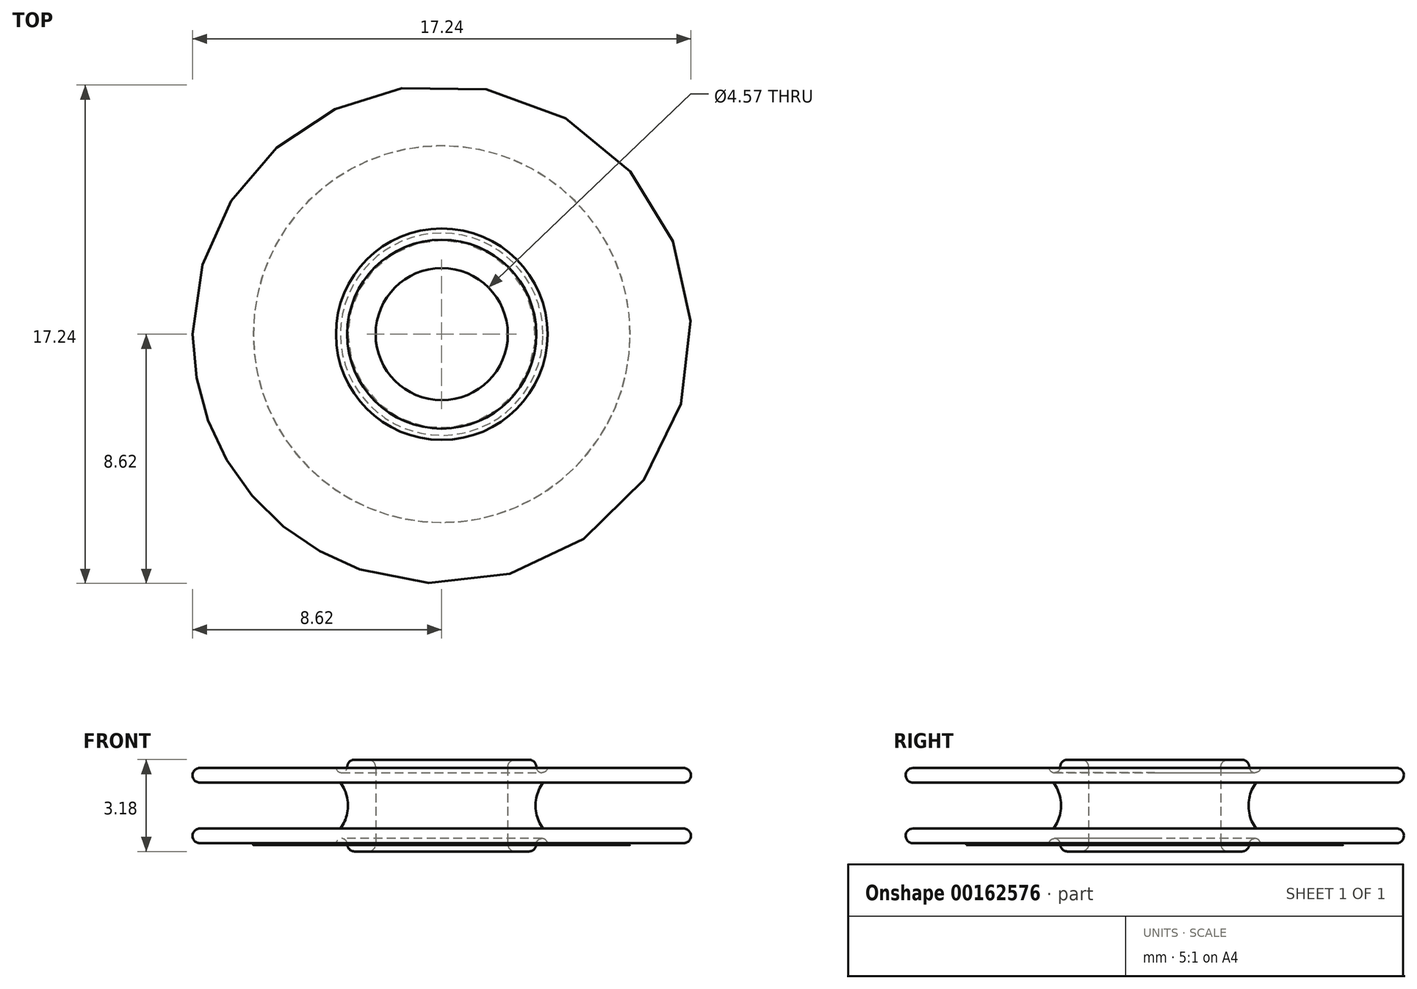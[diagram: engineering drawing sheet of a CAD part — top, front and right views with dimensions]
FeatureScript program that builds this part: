
annotation { "Feature Type Name" : "Feature", "Feature Type Description" : "" }
export const myFeature = defineFeature(function(context is Context, id is Id, definition is map)
    precondition{}
    {
        {
            var Q0;
            Q0=qCreatedBy(makeId("Front.planeOp"),FACE);
            var sketch = newSketch(context, id + "F0", { "sketchPlane" : qUnion([Q0])});
            skPoint(sketch, "E0.end.orphan", {"position": v(8.13, 3.13) * mm});
            skPoint(sketch, "E1.start.orphan", {"position": v(1.92, 6.45) * mm});
            skPoint(sketch, "E2.orphan", {"position": v(1.92, 3.4) * mm});
            skLineSegment(sketch, "E3", {"start": v(10.16, 2.03) * mm, "end": v(10.16, 2.03) * mm});
            skPoint(sketch, "E4.orphan", {"position": v(8.13, 0) * mm});
            skPoint(sketch, "E5.end.orphan", {"position": v(-8.13, 0) * mm});
            skPoint(sketch, "E6.visualSharp", {"position": v(2.67, 2.67) * mm});
            skPoint(sketch, "E7.visualSharp", {"position": v(1.3, 4.1) * mm});
            skPoint(sketch, "E8.visualSharp", {"position": v(10.16, 2.03) * mm});
            skPoint(sketch, "E9.visualSharp", {"position": v(1.3, 0.1) * mm});
            skLineSegment(sketch, "E10", {"start": v(1.56, 4.1) * mm, "end": v(1.56, 4.1) * mm});
            skLineSegment(sketch, "E11", {"start": v(2.92, 1.7) * mm, "end": v(2.92, 1.7) * mm});
            skPoint(sketch, "E12.visualSharp", {"position": v(2.43, 4.1) * mm});
            skPoint(sketch, "E13.end.orphan", {"position": v(5.24, 0.6) * mm});
            skPoint(sketch, "E13.start.orphan", {"position": v(5.24, -0.32) * mm});
            skLineSegment(sketch, "E14", {"start": v(2.29, 2.92) * mm, "end": v(2.29, 0.25) * mm});
            skLineSegment(sketch, "E15", {"start": v(3.02, 3.18) * mm, "end": v(2.54, 3.18) * mm});
            skArc(sketch, "E16.filletArc", {"start": v(3.27, 2.92) * mm, "mid": v(3.2, 3.1) * mm, "end": v(3.02, 3.18) * mm});
            skPoint(sketch, "E17.visualSharp", {"position": v(2.29, 3.18) * mm});
            skArc(sketch, "E17.filletArc", {"start": v(2.54, 3.18) * mm, "mid": v(2.36, 3.1) * mm, "end": v(2.29, 2.92) * mm});
            skPoint(sketch, "E18.orphan", {"position": v(5.7, 4.63) * mm});
            skPoint(sketch, "E19.orphan", {"position": v(5.7, 4.44) * mm});
            skLineSegment(sketch, "E20", {"start": v(6.52, 0.24) * mm, "end": v(6.51, 0.22) * mm});
            skPoint(sketch, "E21.visualSharp", {"position": v(2.29, 0) * mm});
            skPoint(sketch, "E22.visualSharp", {"position": v(3.24, 0) * mm});
            skPoint(sketch, "E23.visualSharp", {"position": v(3.27, 2.68) * mm});
            skPoint(sketch, "E24.visualSharp", {"position": v(3.38, 1.58) * mm});
            skPoint(sketch, "E25.visualSharp", {"position": v(3.24, 1.24) * mm});
            skPoint(sketch, "E26.visualSharp", {"position": v(9.55, 4.38) * mm});
            skPoint(sketch, "E27.visualSharp", {"position": v(9.7, 4.34) * mm});
            skPoint(sketch, "E28.visualSharp", {"position": v(6.6, 0.46) * mm});
            skArc(sketch, "E28.filletArc", {"start": v(6.51, 0.22) * mm, "mid": v(6.51, 0.22) * mm, "end": v(6.52, 0.23) * mm});
            skPoint(sketch, "E29.visualSharp", {"position": v(6.44, 0) * mm});
            skArc(sketch, "E29.filletArc", {"start": v(6.52, 0.23) * mm, "mid": v(6.52, 0.23) * mm, "end": v(6.52, 0.24) * mm});
            skLineSegment(sketch, "E30", {"start": v(8.36, 2.9) * mm, "end": v(3.66, 2.9) * mm});
            skArc(sketch, "E31", {"start": v(8.36, 2.38) * mm, "mid": v(8.62, 2.64) * mm, "end": v(8.36, 2.9) * mm});
            skLineSegment(sketch, "E32", {"start": v(8.36, 2.38) * mm, "end": v(3.5, 2.38) * mm});
            skPoint(sketch, "E33.orphan", {"position": v(8.64, 2.9) * mm});
            skArc(sketch, "E34", {"start": v(3.22, 1.26) * mm, "mid": v(3.23, 1.25) * mm, "end": v(3.24, 1.24) * mm});
            skArc(sketch, "E35", {"start": v(3.27, 2.92) * mm, "mid": v(3.45, 2.73) * mm, "end": v(3.66, 2.9) * mm});
            skLineSegment(sketch, "E36.MirrorCS", {"start": v(8.36, 0.8) * mm, "end": v(3.5, 0.8) * mm});
            skLineSegment(sketch, "E37.MirrorCS", {"start": v(8.36, 0.28) * mm, "end": v(3.66, 0.28) * mm});
            skArc(sketch, "E38.MirrorCS", {"start": v(8.36, 0.8) * mm, "mid": v(8.62, 0.54) * mm, "end": v(8.36, 0.28) * mm});
            skArc(sketch, "E39", {"start": v(3.5, 2.38) * mm, "mid": v(3.24, 1.59) * mm, "end": v(3.5, 0.8) * mm});
            skLineSegment(sketch, "E40", {"start": v(2.29, 1.59) * mm, "end": v(9.26, 1.59) * mm});
            skPoint(sketch, "E40.endSnap0", {"position": v(2.29, 1.59) * mm});
            skArc(sketch, "E41.MirrorCS", {"start": v(2.54, 0) * mm, "mid": v(2.36, 0.07) * mm, "end": v(2.29, 0.25) * mm});
            skLineSegment(sketch, "E42.MirrorCS", {"start": v(3.02, 0) * mm, "end": v(2.54, 0) * mm});
            skArc(sketch, "E43.MirrorCS", {"start": v(3.27, 0.25) * mm, "mid": v(3.2, 0.07) * mm, "end": v(3.02, 0) * mm});
            skPoint(sketch, "E44.MirrorP", {"position": v(3.27, 0.5) * mm});
            skArc(sketch, "E45.MirrorCS", {"start": v(3.27, 0.25) * mm, "mid": v(3.45, 0.45) * mm, "end": v(3.66, 0.28) * mm});
            skSolve(sketch);
        }
        {
            var Q0;
            Q0 = qSketchRegion(id + "F0", true);
            var sketch = newSketch(context, id + "F1", { "sketchPlane" : qUnion([Q0])});
            skLineSegment(sketch, "E46", {"start": v(0, 0) * mm, "end": v(0, 9) * mm});
            skSolve(sketch);
        }
        {
            var Q0;
            Q0 = qSketchRegion(id + "F0", true);
            var Q1;
            Q1 = qBodyType(qCreatedBy(id + "F1" ,EDGE), BodyType.WIRE);
            revolve(context, id + "F2", {"entities" : qUnion([Q0]), "axis" : qUnion([Q1]), "revolveType" : RevolveType.FULL});
        }
    });
